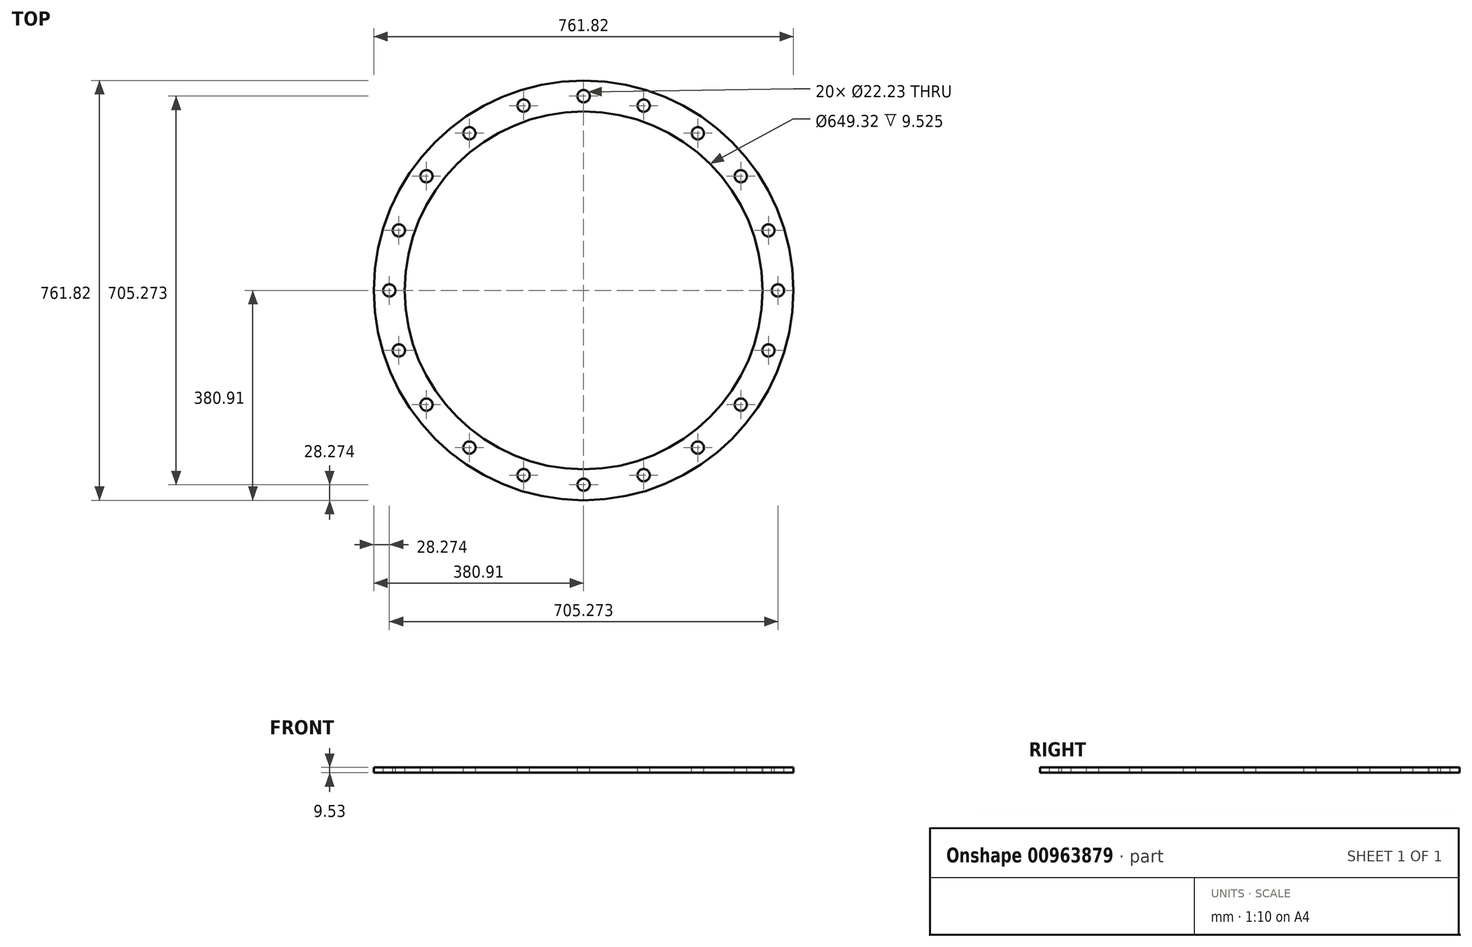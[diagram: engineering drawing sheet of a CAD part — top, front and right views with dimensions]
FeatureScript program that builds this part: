
annotation { "Feature Type Name" : "Feature", "Feature Type Description" : "" }
export const myFeature = defineFeature(function(context is Context, id is Id, definition is map)
    precondition{}
    {
        {
            var Q0;
            Q0=qCreatedBy(makeId("Top.planeOp"),FACE);
            var sketch = newSketch(context, id + "F0", { "sketchPlane" : qUnion([Q0])});
            skCircle(sketch, "E0", {"center": v(0, 0) * mm, "radius": 324.66 * mm});
            skCircle(sketch, "E1", {"center": v(0, 0) * mm, "radius": 380.91 * mm});
            skSolve(sketch);
        }
        {
            var Q0;
            Q0=makeQuery(id+"F0.imprint","IMPRINT",FACE,{"disambiguationData":[TD([[makeQuery(id+"F0.imprint","IMPRINT",EDGE,{"derivedFrom":sQuery(id+"F0.wireOp",EDGE,"E0")}),1.0]])]});
            var sketch = newSketch(context, id + "F1", { "sketchPlane" : qUnion([Q0])});
            skSolve(sketch);
        }
        {
            var Q0;
            Q0=makeQuery(id+"F1.imprint","IMPRINT",FACE,{"disambiguationData":[TD([[makeQuery(id+"F1.imprint","IMPRINT",EDGE,{"derivedFrom":sQuery(id+"F1.wireOp",EDGE,"Ysex6G3V-g2v3-L1Ea-q1q4-sqXVveXDekI2")}),-1.0]])]});
            var Q1;
            Q1=makeQuery(id+"F0.imprint","IMPRINT",FACE,{"disambiguationData":[TD([[makeQuery(id+"F0.imprint","IMPRINT",EDGE,{"derivedFrom":sQuery(id+"F0.wireOp",EDGE,"E0")}),-1.0]])]});
            extrude(context, id + "F2", {"entities" : qUnion([Q0, Q1]), "depth" : 9.52 * mm, "offsetDistance" : 25.4 * mm});
        }
        {
            var Q0;
            Q0=makeQuery(id+"F0.imprint","IMPRINT",FACE,{"disambiguationData":[TD([[makeQuery(id+"F0.imprint","IMPRINT",EDGE,{"derivedFrom":sQuery(id+"F0.wireOp",EDGE,"E0")}),-1.0]])]});
            var sketch = newSketch(context, id + "F3", { "sketchPlane" : qUnion([Q0])});
            skCircle(sketch, "E2", {"center": v(-352.64, 0) * mm, "radius": 11.13 * mm});
            skCircle(sketch, "E3.1.0", {"center": v(-335.38, -108.97) * mm, "radius": 11.13 * mm});
            skCircle(sketch, "E3.2.0", {"center": v(-285.29, -207.27) * mm, "radius": 11.13 * mm});
            skPoint(sketch, "E3.center", {"position": v(0, 0) * mm});
            skCircle(sketch, "E4.1.3.0", {"center": v(-207.27, -285.29) * mm, "radius": 11.13 * mm});
            skCircle(sketch, "E4.1.4.0", {"center": v(-108.97, -335.38) * mm, "radius": 11.13 * mm});
            skCircle(sketch, "E4.1.5.0", {"center": v(0, -352.64) * mm, "radius": 11.13 * mm});
            skCircle(sketch, "E4.1.6.0", {"center": v(108.97, -335.38) * mm, "radius": 11.13 * mm});
            skCircle(sketch, "E4.1.7.0", {"center": v(207.27, -285.29) * mm, "radius": 11.13 * mm});
            skCircle(sketch, "E4.1.8.0", {"center": v(285.29, -207.27) * mm, "radius": 11.13 * mm});
            skCircle(sketch, "E4.1.9.0", {"center": v(335.38, -108.97) * mm, "radius": 11.13 * mm});
            skCircle(sketch, "E4.1.10.0", {"center": v(352.64, 0) * mm, "radius": 11.13 * mm});
            skCircle(sketch, "E4.1.11.0", {"center": v(335.38, 108.97) * mm, "radius": 11.13 * mm});
            skCircle(sketch, "E4.1.12.0", {"center": v(285.29, 207.27) * mm, "radius": 11.13 * mm});
            skCircle(sketch, "E4.1.13.0", {"center": v(207.27, 285.29) * mm, "radius": 11.13 * mm});
            skCircle(sketch, "E4.1.14.0", {"center": v(108.97, 335.38) * mm, "radius": 11.13 * mm});
            skCircle(sketch, "E4.1.15.0", {"center": v(0, 352.64) * mm, "radius": 11.13 * mm});
            skCircle(sketch, "E4.1.16.0", {"center": v(-108.97, 335.38) * mm, "radius": 11.13 * mm});
            skCircle(sketch, "E4.1.17.0", {"center": v(-207.27, 285.29) * mm, "radius": 11.13 * mm});
            skCircle(sketch, "E4.1.18.0", {"center": v(-285.29, 207.27) * mm, "radius": 11.13 * mm});
            skCircle(sketch, "E4.1.19.0", {"center": v(-335.38, 108.97) * mm, "radius": 11.13 * mm});
            skSolve(sketch);
        }
        {
            var Q0;
            Q0=sQuery(id+"F3.wireOp",EDGE,"E4.1.17.0");
            var Q1;
            Q1=sQuery(id+"F3.wireOp",EDGE,"E4.1.18.0");
            var Q2;
            Q2=sQuery(id+"F3.wireOp",EDGE,"E4.1.19.0");
            var Q3;
            Q3=sQuery(id+"F3.wireOp",EDGE,"E2");
            var Q4;
            Q4=sQuery(id+"F3.wireOp",EDGE,"E3.1.0");
            var Q5;
            Q5=sQuery(id+"F3.wireOp",EDGE,"E3.2.0");
            var Q6;
            Q6=sQuery(id+"F3.wireOp",EDGE,"E4.1.3.0");
            var Q7;
            Q7=sQuery(id+"F3.wireOp",EDGE,"E4.1.4.0");
            var Q8;
            Q8=sQuery(id+"F3.wireOp",EDGE,"E4.1.5.0");
            var Q9;
            Q9=sQuery(id+"F3.wireOp",EDGE,"E4.1.6.0");
            var Q10;
            Q10=sQuery(id+"F3.wireOp",EDGE,"E4.1.7.0");
            var Q11;
            Q11=sQuery(id+"F3.wireOp",EDGE,"E4.1.8.0");
            var Q12;
            Q12=sQuery(id+"F3.wireOp",EDGE,"E4.1.9.0");
            var Q13;
            Q13=sQuery(id+"F3.wireOp",EDGE,"E4.1.10.0");
            var Q14;
            Q14=sQuery(id+"F3.wireOp",EDGE,"E4.1.11.0");
            var Q15;
            Q15=sQuery(id+"F3.wireOp",EDGE,"E4.1.12.0");
            var Q16;
            Q16=sQuery(id+"F3.wireOp",EDGE,"E4.1.13.0");
            var Q17;
            Q17=sQuery(id+"F3.wireOp",EDGE,"E4.1.14.0");
            var Q18;
            Q18=sQuery(id+"F3.wireOp",EDGE,"E4.1.15.0");
            var Q19;
            Q19=sQuery(id+"F3.wireOp",EDGE,"E4.1.16.0");
            extrude(context, id + "F4", {"bodyType" : ExtendedToolBodyType.SURFACE, "surfaceEntities" : qUnion([Q0, Q1, Q2, Q3, Q4, Q5, Q6, Q7, Q8, Q9, Q10, Q11, Q12, Q13, Q14, Q15, Q16, Q17, Q18, Q19]), "oppositeDirection" : true, "depth" : 9.52 * mm, "offsetDistance" : 25.4 * mm});
        }
        {
            var Q0;
            Q0=sQuery(id+"F3.wireOp",VERTEX,"E4.1.18.0.center");
            var Q1;
            Q1=sQuery(id+"F3.wireOp",VERTEX,"E4.1.19.0.center");
            var Q2;
            Q2=sQuery(id+"F3.wireOp",VERTEX,"E2.center");
            var Q3;
            Q3=sQuery(id+"F3.wireOp",VERTEX,"E3.1.0.center");
            var Q4;
            Q4=sQuery(id+"F3.wireOp",VERTEX,"E3.2.0.center");
            var Q5;
            Q5=sQuery(id+"F3.wireOp",VERTEX,"E4.1.3.0.center");
            var Q6;
            Q6=sQuery(id+"F3.wireOp",VERTEX,"E4.1.4.0.center");
            var Q7;
            Q7=sQuery(id+"F3.wireOp",VERTEX,"E4.1.5.0.center");
            var Q8;
            Q8=sQuery(id+"F3.wireOp",VERTEX,"E4.1.6.0.center");
            var Q9;
            Q9=sQuery(id+"F3.wireOp",VERTEX,"E4.1.7.0.center");
            var Q10;
            Q10=sQuery(id+"F3.wireOp",VERTEX,"E4.1.8.0.center");
            var Q11;
            Q11=sQuery(id+"F3.wireOp",VERTEX,"E4.1.9.0.center");
            var Q12;
            Q12=sQuery(id+"F3.wireOp",VERTEX,"E4.1.10.0.center");
            var Q13;
            Q13=sQuery(id+"F3.wireOp",VERTEX,"E4.1.11.0.center");
            var Q14;
            Q14=sQuery(id+"F3.wireOp",VERTEX,"E4.1.12.0.center");
            var Q15;
            Q15=sQuery(id+"F3.wireOp",VERTEX,"E4.1.13.0.center");
            var Q16;
            Q16=sQuery(id+"F3.wireOp",VERTEX,"E4.1.14.0.center");
            var Q17;
            Q17=sQuery(id+"F3.wireOp",VERTEX,"E4.1.15.0.center");
            var Q18;
            Q18=sQuery(id+"F3.wireOp",VERTEX,"E4.1.16.0.center");
            var Q19;
            Q19=sQuery(id+"F3.wireOp",VERTEX,"E4.1.17.0.center");
            var Q20;
            Q20=makeQuery(id+"F2.opExtrude","SWEPT_BODY",BODY,{"disambiguationData":[OSD([sQuery(id+"F0.wireOp",EDGE,"E0"),sQuery(id+"F0.wireOp",EDGE,"E1")])]});
            hole(context, id + "F5", {"style" : HoleStyle.SIMPLE, "endStyle" : HoleEndStyle.THROUGH, "oppositeDirection" : true, "holeDiameter" : 22.22 * mm, "majorDiameter" : 6.35 * mm, "isTappedThrough" : true, "tappedDepth" : 12.7 * mm, "tapClearance" : 3, "locations" : qUnion([Q0, Q1, Q2, Q3, Q4, Q5, Q6, Q7, Q8, Q9, Q10, Q11, Q12, Q13, Q14, Q15, Q16, Q17, Q18, Q19]), "scope" : qUnion([Q20]), "startStyle" : HoleStartStyle.PART});
        }
    });
